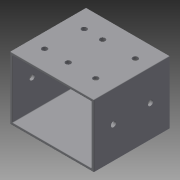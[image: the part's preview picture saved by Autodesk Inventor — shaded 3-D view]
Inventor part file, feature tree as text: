
AUTODESK INVENTOR PART (.ipt)
format: ipt  version: 2014 (Build 180170000, 170)  size: 180,224 bytes
history: native  units: in
note: dims shown in document units (in); Inventor stores cm internally (conversion verified against a paired STEP export)
features: extrude x4, sketch x4, shell x1, fillet x1
ambient origin geometry x8: Origin, YZ Plane, XZ Plane, XY Plane, X Axis, Y Axis, Z Axis, Center Point
bodies: Solid1 (feature_tree)
feature tree (10):
  extrude  "Extrusion1"  Depth=0.5in
  shell  "Shell1"  Thickness=3.0in
  fillet  "Fillet1"  Radius=3.0in
  extrude  "Extrusion6"  Depth=1.8125in
  sketch  "Sketch10"  dims[d87=0.0in d106=0.5in]
  extrude  "Extrusion7"  Depth=0.5in
  extrude  "Extrusion8"  Depth=0.25in
  sketch  "Sketch1"  dims[d3=0.0in d81=0.5in d82=3.0in d83=3.0in]
  sketch  "Sketch9"  dims[d84=1.8125in d85=1.8125in]
  sketch  "Sketch11"  dims[d107=0.5in d108=1.8125in d109=1.8125in d110=3.0in d111=3.0in d112=0.5in d113=0.5in d114=0.5in d115=1.8125in d116=1.8125in d117=1.8125in d118=0.5in d119=0.5in d120=0.5in d121=1.6375in d122=4.875in d123=3.125in d124=2.25in d125=2.625in d126=1.8125in d127=1.8125in d128=1.8125in d129=1.6375in d130=0.25in d131=0.0in d132=0.25in d133=0.0in]
